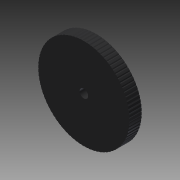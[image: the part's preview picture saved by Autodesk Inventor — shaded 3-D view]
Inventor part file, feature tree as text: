
AUTODESK INVENTOR PART (.ipt)
format: ipt  version: 2014 (Build 180170000, 170)  size: 278,016 bytes
history: native  units: mm
features: extrude x3, sketch x3, pattern_circular x1
ambient origin geometry x8: Origin, YZ Plane, XZ Plane, XY Plane, X Axis, Y Axis, Z Axis, Center Point
bodies: Solid1 (feature_tree)
feature tree (7):
  extrude  "Extrusion1"  Depth=10.0mm TaperAngle=0.0deg
  extrude  "Extrusion2"  Depth=10.0mm TaperAngle=0.0deg
  extrude  "Extrusion3"  Depth=10.0mm TaperAngle=360.0deg
  pattern_circular  "Circular Pattern1"  [2 undecoded]
  sketch  "Sketch1"  dims[d0=74.0mm d1=10.0mm d2=0.0mm]
  sketch  "Sketch2"  dims[d3=7.0mm d4=10.0mm d5=0.0mm]
  sketch  "Sketch3"  dims[d7=10.0mm d8=0.0mm d9=800.0mm d10=360.0deg]
note: 2 required parameter values undecoded (feature->parameter linkage not recoverable at this tier; creation-order binding heuristic only, values carry confidence <= 0.55)
